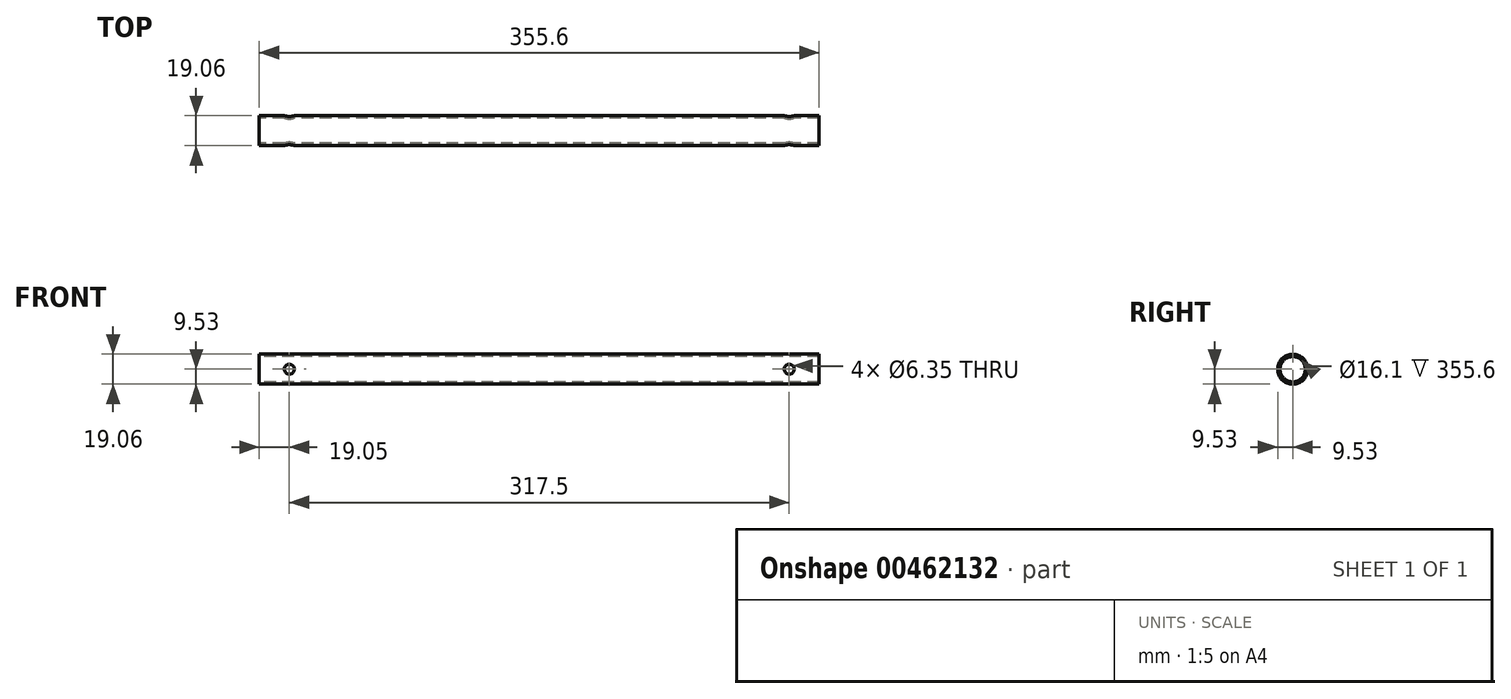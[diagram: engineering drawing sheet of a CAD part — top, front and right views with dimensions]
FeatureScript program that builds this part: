
annotation { "Feature Type Name" : "Feature", "Feature Type Description" : "" }
export const myFeature = defineFeature(function(context is Context, id is Id, definition is map)
    precondition{}
    {
        {
            var Q0;
            Q0=qCreatedBy(makeId("Right.planeOp"),FACE);
            var sketch = newSketch(context, id + "F0", { "sketchPlane" : qUnion([Q0])});
            skCircle(sketch, "E0", {"center": v(0, 0) * mm, "radius": 9.53 * mm});
            skCircle(sketch, "E1.0", {"center": v(0, 0) * mm, "radius": 8.05 * mm});
            skSolve(sketch);
        }
        {
            var Q0;
            Q0 = qSketchRegion(id + "F0", true);
            extrude(context, id + "F1", {"entities" : qUnion([Q0]), "depth" : 355.6 * mm});
        }
        {
            var Q0;
            Q0=qCreatedBy(makeId("Front.planeOp"),FACE);
            var sketch = newSketch(context, id + "F2", { "sketchPlane" : qUnion([Q0])});
            skLineSegment(sketch, "E2", {"start": v(254.88, 0) * mm, "end": v(-76.65, 0) * mm, "construction": true});
            skCircle(sketch, "E3", {"center": v(336.55, 0) * mm, "radius": 3.17 * mm});
            skCircle(sketch, "E4", {"center": v(19.05, 0) * mm, "radius": 3.18 * mm});
            skSolve(sketch);
        }
        {
            var Q0;
            Q0 = qSketchRegion(id + "F2", true);
            extrude(context, id + "F3", {"entities" : qUnion([Q0]), "operationType" : NewBodyOperationType.REMOVE, "oppositeDirection" : true, "depth" : 76.2 * mm, "symmetric" : true});
        }
    });
